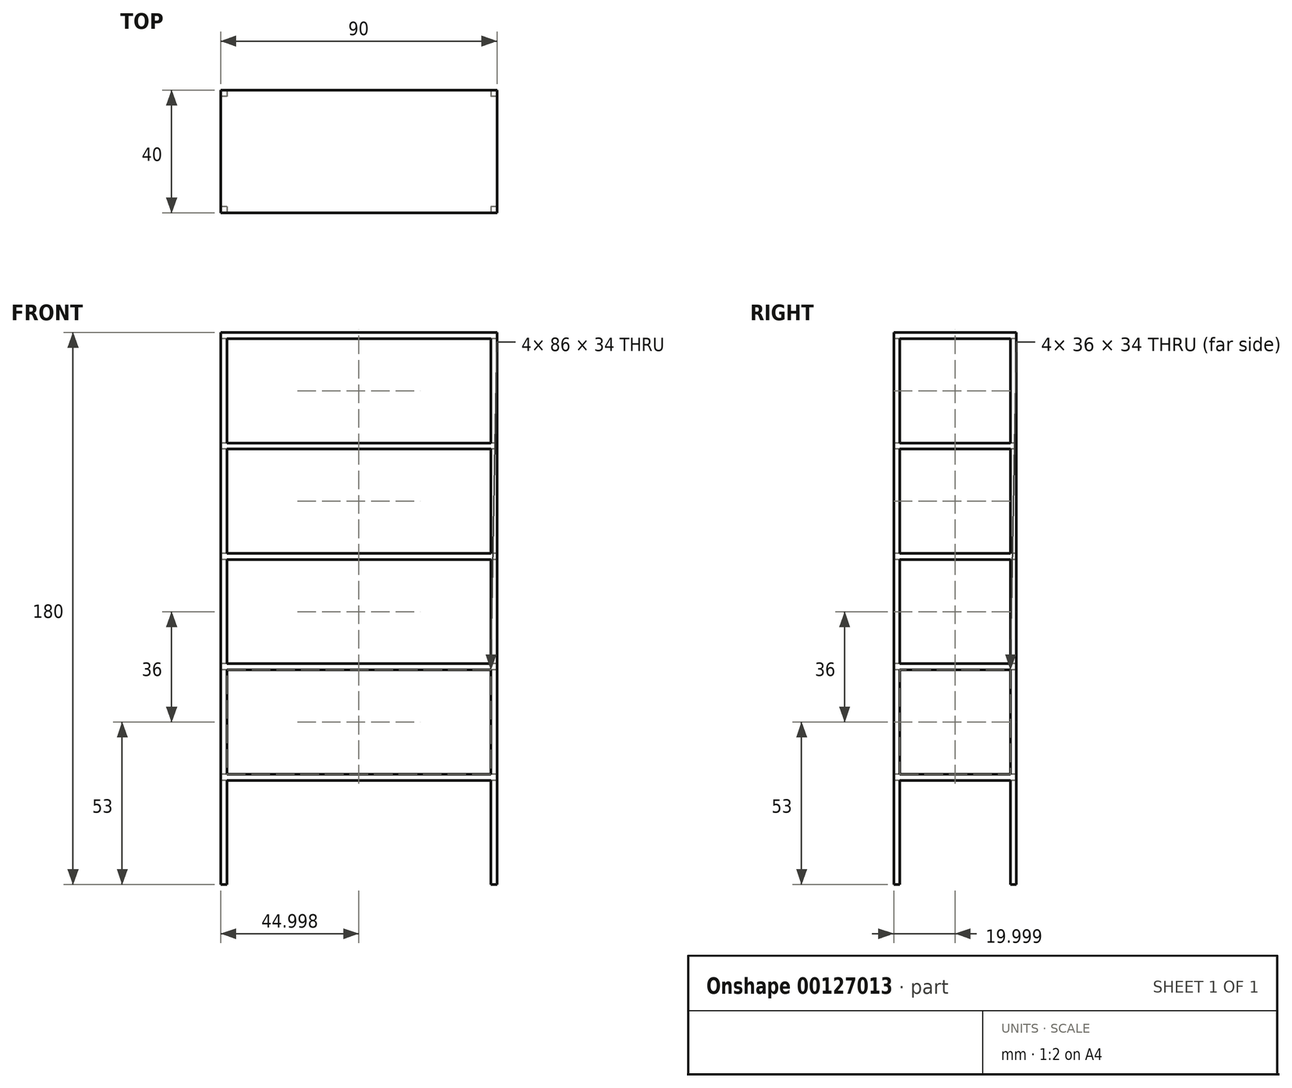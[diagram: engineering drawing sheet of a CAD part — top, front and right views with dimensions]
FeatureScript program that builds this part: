
annotation { "Feature Type Name" : "Feature", "Feature Type Description" : "" }
export const myFeature = defineFeature(function(context is Context, id is Id, definition is map)
    precondition{}
    {
        {
            var Q0;
            Q0=qCreatedBy(makeId("Top.planeOp"),FACE);
            var sketch = newSketch(context, id + "F0", { "sketchPlane" : qUnion([Q0])});
            skLineSegment(sketch, "E0.bottom", {"start": v(-34.53, 17.07) * mm, "end": v(55.47, 17.07) * mm});
            skLineSegment(sketch, "E0.top", {"start": v(-34.53, -22.93) * mm, "end": v(55.47, -22.93) * mm});
            skLineSegment(sketch, "E0.left", {"start": v(-34.53, 17.07) * mm, "end": v(-34.53, -22.93) * mm});
            skLineSegment(sketch, "E0.right", {"start": v(55.47, 17.07) * mm, "end": v(55.47, -22.93) * mm});
            skSolve(sketch);
        }
        {
            var Q0;
            Q0 = qSketchRegion(id + "F0", true);
            extrude(context, id + "F1", {"entities" : qUnion([Q0]), "depth" : 180 * mm});
        }
        {
            var Q0;
            Q0=makeQuery(id+"F1.opExtrude","SWEPT_FACE",FACE,{"disambiguationData":[OSD([sQuery(id+"F0.wireOp",EDGE,"E0.top")])]});
            var sketch = newSketch(context, id + "F2", { "sketchPlane" : qUnion([Q0])});
            skLineSegment(sketch, "E1.bottom", {"start": v(-32.53, 178) * mm, "end": v(53.47, 178) * mm});
            skLineSegment(sketch, "E1.top", {"start": v(-32.53, 144) * mm, "end": v(53.47, 144) * mm});
            skLineSegment(sketch, "E1.left", {"start": v(-32.53, 178) * mm, "end": v(-32.53, 144) * mm});
            skLineSegment(sketch, "E1.right", {"start": v(53.47, 178) * mm, "end": v(53.47, 144) * mm});
            skLineSegment(sketch, "E2.0.1.0", {"start": v(-32.53, 142) * mm, "end": v(53.47, 142) * mm});
            skLineSegment(sketch, "E2.0.1.1", {"start": v(-32.53, 142) * mm, "end": v(-32.53, 108) * mm});
            skLineSegment(sketch, "E2.0.1.2", {"start": v(-32.53, 108) * mm, "end": v(53.47, 108) * mm});
            skLineSegment(sketch, "E2.0.1.3", {"start": v(53.47, 142) * mm, "end": v(53.47, 108) * mm});
            skLineSegment(sketch, "E2.0.2.0", {"start": v(-32.53, 106) * mm, "end": v(53.47, 106) * mm});
            skLineSegment(sketch, "E2.0.2.1", {"start": v(-32.53, 106) * mm, "end": v(-32.53, 72) * mm});
            skLineSegment(sketch, "E2.0.2.2", {"start": v(-32.53, 72) * mm, "end": v(53.47, 72) * mm});
            skLineSegment(sketch, "E2.0.2.3", {"start": v(53.47, 106) * mm, "end": v(53.47, 72) * mm});
            skLineSegment(sketch, "E2.0.3.0", {"start": v(-32.53, 70) * mm, "end": v(53.47, 70) * mm});
            skLineSegment(sketch, "E2.0.3.1", {"start": v(-32.53, 70) * mm, "end": v(-32.53, 36) * mm});
            skLineSegment(sketch, "E2.0.3.2", {"start": v(-32.53, 36) * mm, "end": v(53.47, 36) * mm});
            skLineSegment(sketch, "E2.0.3.3", {"start": v(53.47, 70) * mm, "end": v(53.47, 36) * mm});
            skLineSegment(sketch, "E2.0.4.0", {"start": v(-32.53, 34) * mm, "end": v(53.47, 34) * mm});
            skLineSegment(sketch, "E2.0.4.1", {"start": v(-32.53, 34) * mm, "end": v(-32.53, 0) * mm});
            skLineSegment(sketch, "E2.0.4.2", {"start": v(-32.53, 0) * mm, "end": v(53.47, 0) * mm});
            skLineSegment(sketch, "E2.0.4.3", {"start": v(53.47, 34) * mm, "end": v(53.47, 0) * mm});
            skLineSegment(sketch, "E2.direction1", {"start": v(-32.53, 178) * mm, "end": v(-7.53, 178) * mm, "construction": true});
            skLineSegment(sketch, "E2.direction2", {"start": v(-32.53, 178) * mm, "end": v(-32.53, 142) * mm, "construction": true});
            skSolve(sketch);
        }
        {
            var Q0;
            Q0=makeQuery(id+"F2.imprint","IMPRINT",FACE,{"disambiguationData":[TD([[makeQuery(id+"F2.imprint","IMPRINT",EDGE,{"derivedFrom":sQuery(id+"F2.wireOp",EDGE,"E1.bottom")}),-1.0]])]});
            var Q1;
            Q1=makeQuery(id+"F2.imprint","IMPRINT",FACE,{"disambiguationData":[TD([[makeQuery(id+"F2.imprint","IMPRINT",EDGE,{"derivedFrom":sQuery(id+"F2.wireOp",EDGE,"E2.0.1.0")}),-1.0]])]});
            var Q2;
            Q2=makeQuery(id+"F2.imprint","IMPRINT",FACE,{"disambiguationData":[TD([[makeQuery(id+"F2.imprint","IMPRINT",EDGE,{"derivedFrom":sQuery(id+"F2.wireOp",EDGE,"E2.0.2.0")}),-1.0]])]});
            var Q3;
            Q3=makeQuery(id+"F2.imprint","IMPRINT",FACE,{"disambiguationData":[TD([[makeQuery(id+"F2.imprint","IMPRINT",EDGE,{"derivedFrom":sQuery(id+"F2.wireOp",EDGE,"E2.0.3.0")}),-1.0]])]});
            var Q4;
            Q4=makeQuery(id+"F2.imprint","IMPRINT",FACE,{"disambiguationData":[TD([[makeQuery(id+"F2.imprint","IMPRINT",EDGE,{"derivedFrom":sQuery(id+"F2.wireOp",EDGE,"E2.0.4.0")}),-1.0]])]});
            extrude(context, id + "F3", {"entities" : qUnion([Q0, Q1, Q2, Q3, Q4]), "operationType" : NewBodyOperationType.REMOVE, "endBound" : BoundingType.THROUGH_ALL, "oppositeDirection" : true, "depth" : 25 * mm});
        }
        {
            var Q0;
            Q0=makeQuery(id+"F1.opExtrude","SWEPT_FACE",FACE,{"disambiguationData":[OSD([sQuery(id+"F0.wireOp",EDGE,"E0.left")])]});
            var sketch = newSketch(context, id + "F4", { "sketchPlane" : qUnion([Q0])});
            skLineSegment(sketch, "E3.bottom", {"start": v(-15.07, 178) * mm, "end": v(20.93, 178) * mm});
            skLineSegment(sketch, "E3.top", {"start": v(-15.07, 144) * mm, "end": v(20.93, 144) * mm});
            skLineSegment(sketch, "E3.left", {"start": v(-15.07, 178) * mm, "end": v(-15.07, 144) * mm});
            skLineSegment(sketch, "E3.right", {"start": v(20.93, 178) * mm, "end": v(20.93, 144) * mm});
            skLineSegment(sketch, "E4.0.1.0", {"start": v(-15.07, 142) * mm, "end": v(20.93, 142) * mm});
            skLineSegment(sketch, "E4.0.1.1", {"start": v(-15.07, 142) * mm, "end": v(-15.07, 108) * mm});
            skLineSegment(sketch, "E4.0.1.2", {"start": v(20.93, 142) * mm, "end": v(20.93, 108) * mm});
            skLineSegment(sketch, "E4.0.1.3", {"start": v(-15.07, 108) * mm, "end": v(20.93, 108) * mm});
            skLineSegment(sketch, "E4.0.2.0", {"start": v(-15.07, 106) * mm, "end": v(20.93, 106) * mm});
            skLineSegment(sketch, "E4.0.2.1", {"start": v(-15.07, 106) * mm, "end": v(-15.07, 72) * mm});
            skLineSegment(sketch, "E4.0.2.2", {"start": v(20.93, 106) * mm, "end": v(20.93, 72) * mm});
            skLineSegment(sketch, "E4.0.2.3", {"start": v(-15.07, 72) * mm, "end": v(20.93, 72) * mm});
            skLineSegment(sketch, "E4.0.3.0", {"start": v(-15.07, 70) * mm, "end": v(20.93, 70) * mm});
            skLineSegment(sketch, "E4.0.3.1", {"start": v(-15.07, 70) * mm, "end": v(-15.07, 36) * mm});
            skLineSegment(sketch, "E4.0.3.2", {"start": v(20.93, 70) * mm, "end": v(20.93, 36) * mm});
            skLineSegment(sketch, "E4.0.3.3", {"start": v(-15.07, 36) * mm, "end": v(20.93, 36) * mm});
            skLineSegment(sketch, "E4.0.4.0", {"start": v(-15.07, 34) * mm, "end": v(20.93, 34) * mm});
            skLineSegment(sketch, "E4.0.4.1", {"start": v(-15.07, 34) * mm, "end": v(-15.07, 0) * mm});
            skLineSegment(sketch, "E4.0.4.2", {"start": v(20.93, 34) * mm, "end": v(20.93, 0) * mm});
            skLineSegment(sketch, "E4.0.4.3", {"start": v(-15.07, 0) * mm, "end": v(20.93, 0) * mm});
            skLineSegment(sketch, "E4.direction1", {"start": v(-15.07, 178) * mm, "end": v(9.93, 178) * mm, "construction": true});
            skLineSegment(sketch, "E4.direction2", {"start": v(-15.07, 178) * mm, "end": v(-15.07, 142) * mm, "construction": true});
            skSolve(sketch);
        }
        {
            var Q0;
            Q0=makeQuery(id+"F4.imprint","IMPRINT",FACE,{"disambiguationData":[TD([[makeQuery(id+"F4.imprint","IMPRINT",EDGE,{"derivedFrom":sQuery(id+"F4.wireOp",EDGE,"E3.bottom")}),-1.0]])]});
            var Q1;
            Q1=makeQuery(id+"F4.imprint","IMPRINT",FACE,{"disambiguationData":[TD([[makeQuery(id+"F4.imprint","IMPRINT",EDGE,{"derivedFrom":sQuery(id+"F4.wireOp",EDGE,"E4.0.1.0")}),-1.0]])]});
            var Q2;
            Q2=makeQuery(id+"F4.imprint","IMPRINT",FACE,{"disambiguationData":[TD([[makeQuery(id+"F4.imprint","IMPRINT",EDGE,{"derivedFrom":sQuery(id+"F4.wireOp",EDGE,"E4.0.2.0")}),-1.0]])]});
            var Q3;
            Q3=makeQuery(id+"F4.imprint","IMPRINT",FACE,{"disambiguationData":[TD([[makeQuery(id+"F4.imprint","IMPRINT",EDGE,{"derivedFrom":sQuery(id+"F4.wireOp",EDGE,"E4.0.3.0")}),-1.0]])]});
            var Q4;
            Q4=makeQuery(id+"F4.imprint","IMPRINT",FACE,{"disambiguationData":[TD([[makeQuery(id+"F4.imprint","IMPRINT",EDGE,{"derivedFrom":sQuery(id+"F4.wireOp",EDGE,"E4.0.4.0")}),-1.0]])]});
            extrude(context, id + "F5", {"entities" : qUnion([Q0, Q1, Q2, Q3, Q4]), "operationType" : NewBodyOperationType.REMOVE, "endBound" : BoundingType.THROUGH_ALL, "oppositeDirection" : true, "depth" : 25 * mm});
        }
    });
